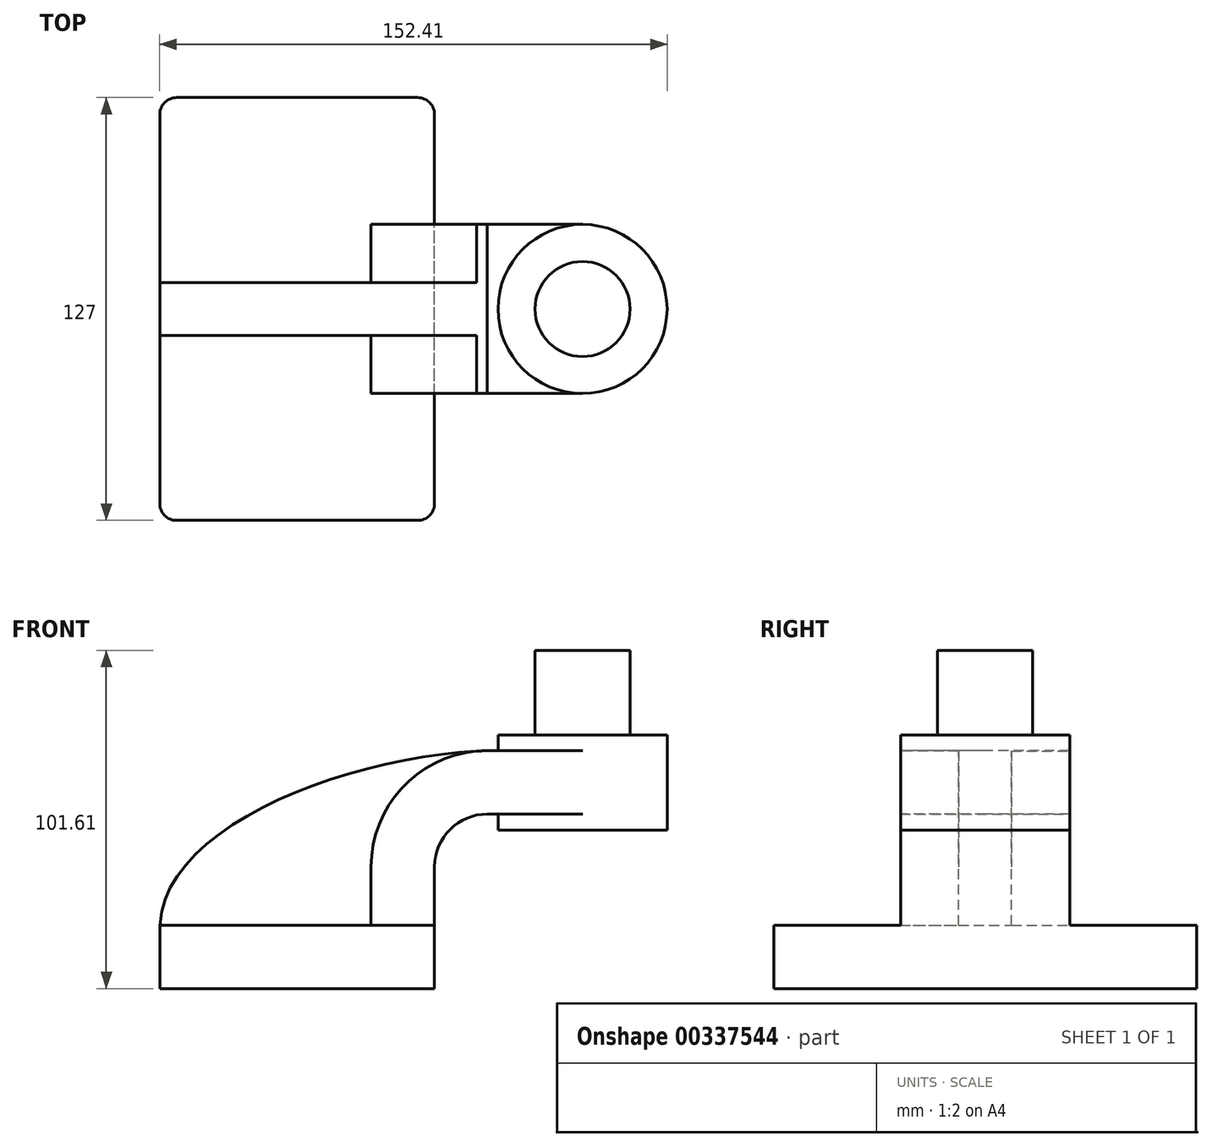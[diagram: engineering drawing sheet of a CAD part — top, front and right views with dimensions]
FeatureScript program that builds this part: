
annotation { "Feature Type Name" : "Feature", "Feature Type Description" : "" }
export const myFeature = defineFeature(function(context is Context, id is Id, definition is map)
    precondition{}
    {
        {
            var Q0;
            Q0=qCreatedBy(makeId("Front.planeOp"),FACE);
            var sketch = newSketch(context, id + "F0", { "sketchPlane" : qUnion([Q0])});
            skLineSegment(sketch, "E0.rect.bottom", {"start": v(-41.28, 9.52) * mm, "end": v(41.28, 9.52) * mm});
            skLineSegment(sketch, "E0.rect.top", {"start": v(-41.28, -9.52) * mm, "end": v(41.28, -9.52) * mm});
            skLineSegment(sketch, "E0.rect.left", {"start": v(-41.28, 9.52) * mm, "end": v(-41.28, -9.52) * mm});
            skLineSegment(sketch, "E0.rect.right", {"start": v(41.28, 9.52) * mm, "end": v(41.28, -9.52) * mm});
            skPoint(sketch, "E0.rect.middle", {"position": v(0, 0) * mm});
            skLineSegment(sketch, "E1", {"start": v(41.28, 9.52) * mm, "end": v(41.28, 27) * mm});
            skArc(sketch, "E2", {"start": v(41.28, 27) * mm, "mid": v(45.92, 38.23) * mm, "end": v(57.15, 42.88) * mm});
            skLineSegment(sketch, "E3", {"start": v(57.15, 42.88) * mm, "end": v(85.72, 42.88) * mm});
            skLineSegment(sketch, "E4.rect.bottom", {"start": v(60.32, 38.1) * mm, "end": v(111.12, 38.1) * mm});
            skLineSegment(sketch, "E4.rect.top", {"start": v(60.32, 66.68) * mm, "end": v(111.12, 66.68) * mm});
            skLineSegment(sketch, "E4.rect.left", {"start": v(60.32, 38.1) * mm, "end": v(60.32, 66.68) * mm});
            skLineSegment(sketch, "E4.rect.right", {"start": v(111.13, 38.1) * mm, "end": v(111.12, 66.68) * mm});
            skPoint(sketch, "E4.rect.middle", {"position": v(85.72, 52.39) * mm});
            skLineSegment(sketch, "E5.0", {"start": v(57.15, 61.93) * mm, "end": v(85.72, 61.93) * mm});
            skArc(sketch, "E5.1", {"start": v(22.23, 27) * mm, "mid": v(32.45, 51.7) * mm, "end": v(57.15, 61.93) * mm});
            skLineSegment(sketch, "E5.2", {"start": v(22.23, 9.52) * mm, "end": v(22.23, 27) * mm});
            skLineSegment(sketch, "E6", {"start": v(85.72, 38.1) * mm, "end": v(85.72, 66.68) * mm});
            skFitSpline(sketch, "E7", {"points": [v(-41.28, 9.53) * mm, v(57.15, 61.93) * mm], "startDerivative": vector(5.2, 92.34) * mm, "endDerivative": vector(120.92, 4.22) * mm});
            skSolve(sketch);
        }
        {
            var Q0;
            Q0=makeQuery(id+"F0.imprint","IMPRINT",FACE,{"disambiguationData":[TD([[makeQuery(id+"F0.imprint","IMPRINT",EDGE,{"derivedFrom":sQuery(id+"F0.wireOp",EDGE,"E0.rect.top")}),1.0]])]});
            extrude(context, id + "F1", {"entities" : qUnion([Q0]), "endBound" : BoundingType.SYMMETRIC, "depth" : 127 * mm});
        }
        {
            var Q0;
            {var subQ9=sQuery(id+"F0.wireOp",EDGE,"E1");Q0=makeQuery(id+"F0.imprint","IMPRINT",FACE,{"disambiguationData":[TD([[makeQuery(id+"F0.imprint","IMPRINT",EDGE,{"derivedFrom":subQ9}),1.0]])]});}
            var Q1;
            {var subQ0=sQuery(id+"F0.wireOp",EDGE,"E6");var subQ1=sQuery(id+"F0.wireOp",EDGE,"E3");var subQ2=makeQuery(id+"F0.imprint","INTERSECT",VERTEX,{"derivedFrom":[subQ1,subQ0]});Q1=makeQuery(id+"F0.imprint","IMPRINT",FACE,{"disambiguationData":[TD([[makeQuery(id+"F0.imprint","IMPRINT",EDGE,{"disambiguationData":[TD([[subQ2,1.0]])],"derivedFrom":subQ1}),1.0]])]});}
            extrude(context, id + "F2", {"entities" : qUnion([Q0, Q1]), "operationType" : NewBodyOperationType.ADD, "endBound" : BoundingType.SYMMETRIC, "depth" : 50.8 * mm});
        }
        {
            var Q0;
            {var subQ3=sQuery(id+"F0.wireOp",EDGE,"E5.2");Q0=makeQuery(id+"F0.imprint","IMPRINT",FACE,{"disambiguationData":[TD([[makeQuery(id+"F0.imprint","IMPRINT",EDGE,{"derivedFrom":subQ3}),1.0]])]});}
            extrude(context, id + "F3", {"entities" : qUnion([Q0]), "operationType" : NewBodyOperationType.ADD, "endBound" : BoundingType.SYMMETRIC, "depth" : 15.88 * mm});
        }
        {
            var Q0;
            {var subQ5=sQuery(id+"F0.wireOp",EDGE,"E4.rect.right");Q0=makeQuery(id+"F0.imprint","IMPRINT",FACE,{"disambiguationData":[TD([[makeQuery(id+"F0.imprint","IMPRINT",EDGE,{"derivedFrom":subQ5}),1.0]])]});}
            var Q1;
            Q1=sQuery(id+"F0.wireOp",EDGE,"E6");
            revolve(context, id + "F4", {"operationType" : NewBodyOperationType.ADD, "entities" : qUnion([Q0]), "axis" : qUnion([Q1]), "revolveType" : RevolveType.FULL});
        }
        {
            var Q0;
            Q0=makeQuery(id+"F1.opExtrude","CAP_EDGE",EDGE,{"disambiguationData":[OSD([sQuery(id+"F0.wireOp",EDGE,"E0.rect.right")])],"isStart":false});
            var Q1;
            Q1=makeQuery(id+"F1.opExtrude","CAP_EDGE",EDGE,{"disambiguationData":[OSD([sQuery(id+"F0.wireOp",EDGE,"E0.rect.left")])],"isStart":false});
            var Q2;
            Q2=makeQuery(id+"F1.opExtrude","CAP_EDGE",EDGE,{"disambiguationData":[OSD([sQuery(id+"F0.wireOp",EDGE,"E0.rect.right")])],"isStart":true});
            var Q3;
            Q3=makeQuery(id+"F1.opExtrude","CAP_EDGE",EDGE,{"disambiguationData":[OSD([sQuery(id+"F0.wireOp",EDGE,"E0.rect.left")])],"isStart":true});
            fillet(context, id + "F5", {"entities" : qUnion([Q0, Q1, Q2, Q3]), "radius" : 5.08 * mm, "tangentPropagation" : true, "allowEdgeOverflow" : false});
        }
        {
            var Q0;
            Q0=makeQuery(id+"F4.opRevolve","SWEPT_FACE",FACE,{"disambiguationData":[OSD([sQuery(id+"F0.wireOp",EDGE,"E4.rect.top")])]});
            var sketch = newSketch(context, id + "F6", { "sketchPlane" : qUnion([Q0])});
            skCircle(sketch, "E8", {"center": v(85.72, 0) * mm, "radius": 14.29 * mm});
            skSolve(sketch);
        }
        {
            var Q0;
            Q0 = qSketchRegion(id + "F6", true);
            extrude(context, id + "F7", {"entities" : qUnion([Q0]), "operationType" : NewBodyOperationType.ADD, "depth" : 25.4 * mm});
        }
    });
